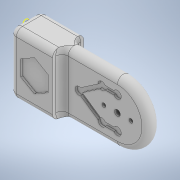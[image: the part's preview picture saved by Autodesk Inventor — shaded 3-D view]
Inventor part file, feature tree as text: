
AUTODESK INVENTOR PART (.ipt)
format: ipt  version: 2022 (Build 260153000, 153)  size: 438,272 bytes
history: native  units: in
note: dims shown in document units (in); Inventor stores cm internally (conversion verified against a paired STEP export)
features: sketch x15, extrude x11, projected_geometry x9, fillet x2, plane x1, mirror x1
ambient origin geometry x8: Origin, YZ Plane, XZ Plane, XY Plane, X Axis, Y Axis, Z Axis, Center Point
bodies: Solid1 (feature_tree)
feature tree (39):
  extrude  "Extrusion1"  Depth=3.937in
  extrude  "Extrusion2"  Depth=0.25in
  sketch  "Sketch3"  dims[d5=0.157in d6=0.157in]
  sketch  "Sketch4"  dims[d7=0.195in d8=0.8in]
  extrude  "Extrusion3"  Depth=0.157in
  extrude  "Extrusion4"  Depth=0.8in
  extrude  "Extrusion5"  Depth=0.157in
  plane  "Work Plane1"
  extrude  "Extrusion7"  Depth=0.0787in
  sketch  "Sketch13"  dims[d19=0.2362in d20=0.0984in d21=0.0984in d22=0.25in d23=0.0in]
  extrude  "Extrusion8"  Depth=0.275in
  extrude  "Extrusion9"  Depth=0.25in TaperAngle=0.0deg
  extrude  "Extrusion10"  Depth=0.25in
  fillet  "Fillet2"  Radius=0.0984in
  fillet  "Fillet3"  Radius=0.25in
  extrude  "Extrusion11"  Depth=1.0in TaperAngle=0.0deg
  extrude  "Extrusion12"  Depth=0.157in
  mirror  "Mirror2"
  sketch  "Sketch19"  dims[d51=0.0in d52=0.0in d58=1.2559in d59=0.0906in d60=0.0906in d61=0.12in d62=0.12in d63=0.4803in d64=0.6299in d65=0.9055in d66=0.626in d67=0.0in d68=0.45in d69=0.626in d70=0.0in d71=0.2362in d72=0.0in d73=0.125in d74=0.125in d75=0.32in d77=0.1575in d78=0.1575in d81=0.0394in d82=0.0394in d84=0.0394in d85=0.0in d86=0.0394in d87=0.0in]
  sketch  "Sketch1"  dims[d0=1.25in d1=3.937in]
  sketch  "Sketch2"  dims[d3=0.25in d4=0.195in]
  projected_geometry  "Projected Loop1"
  projected_geometry  "Projected Loop2"
  sketch  "Sketch5"  dims[d9=1.6in d10=0.157in]
  sketch  "Sketch6"  dims[d11=0.275in d12=0.0787in]
  sketch  "Sketch7"  dims[d13=0.0787in d14=0.275in]
  projected_geometry  "Projected Loop3"
  sketch  "Sketch11"  dims[d15=0.118in d16=0.25in d17=0.0in]
  projected_geometry  "Projected Loop6"
  sketch  "Sketch14"  dims[d24=0.325in d25=1.0in d26=0.0in]
  projected_geometry  "Projected Loop7"
  sketch  "Sketch15"  dims[d27=1.0in d28=0.0in d29=0.157in]
  sketch  "Sketch16"  dims[d30=0.33in]
  projected_geometry  "Projected Loop8"
  projected_geometry  "Projected Loop9"
  sketch  "Sketch17"  dims[d31=0.0in d32=0.0in]
  projected_geometry  "Projected Loop10"
  projected_geometry  "Projected Loop11"
  sketch  "Sketch18"  dims[d50=0.125in]
